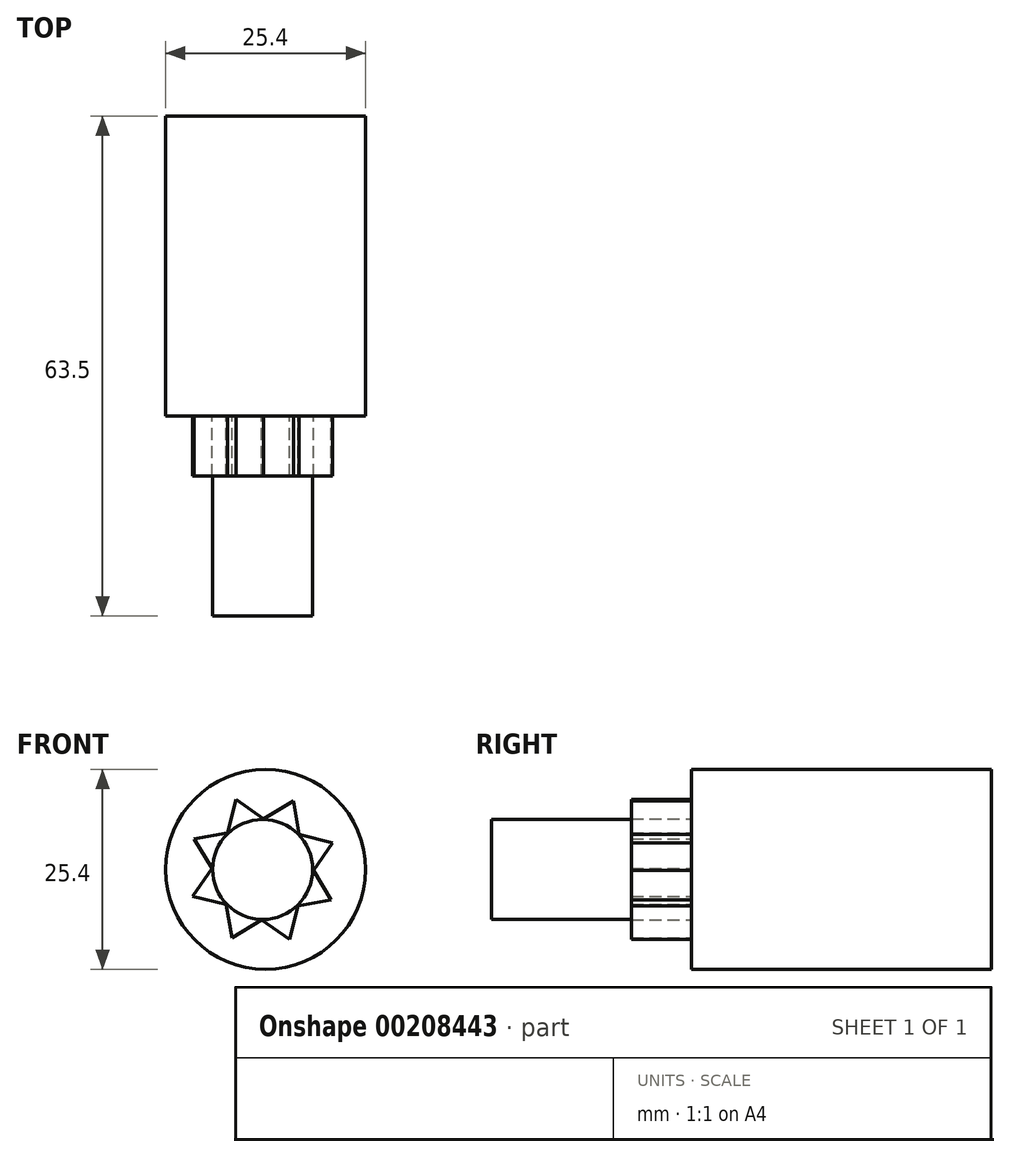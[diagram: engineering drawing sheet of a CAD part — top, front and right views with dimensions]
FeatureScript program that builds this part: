
annotation { "Feature Type Name" : "Feature", "Feature Type Description" : "" }
export const myFeature = defineFeature(function(context is Context, id is Id, definition is map)
    precondition{}
    {
        {
            var Q0;
            Q0=qCreatedBy(makeId("Front.planeOp"),FACE);
            var sketch = newSketch(context, id + "F0", { "sketchPlane" : qUnion([Q0])});
            skCircle(sketch, "E0", {"center": v(0.36, 0) * mm, "radius": 12.7 * mm});
            skSolve(sketch);
        }
        {
            var Q0;
            Q0=makeQuery(id+"F0.imprint","IMPRINT",FACE,{"disambiguationData":[TD([[makeQuery(id+"F0.imprint","IMPRINT",EDGE,{"derivedFrom":sQuery(id+"F0.wireOp",EDGE,"E0")}),1.0]])]});
            extrude(context, id + "F1", {"entities" : qUnion([Q0]), "depth" : 38.1 * mm});
        }
        {
            var Q0;
            Q0=makeQuery(id+"F1.opExtrude","CAP_FACE",FACE,{"disambiguationData":[OSD([sQuery(id+"F0.wireOp",EDGE,"E0")])],"isStart":false});
            var sketch = newSketch(context, id + "F2", { "sketchPlane" : qUnion([Q0])});
            skCircle(sketch, "E1", {"center": v(0, 0) * mm, "radius": 6.35 * mm});
            skSolve(sketch);
        }
        {
            var Q0;
            Q0=qSketchRegion(id+"F2",true);
            extrude(context, id + "F3", {"entities" : qUnion([Q0]), "operationType" : NewBodyOperationType.ADD, "depth" : 25.4 * mm});
        }
        {
            var Q0;
            Q0=makeQuery(id+"F1.opExtrude","CAP_FACE",FACE,{"disambiguationData":[OSD([sQuery(id+"F0.wireOp",EDGE,"E0")])],"isStart":false});
            var sketch = newSketch(context, id + "F4", { "sketchPlane" : qUnion([Q0])});
            skLineSegment(sketch, "E2", {"start": v(-8.7, 3.89) * mm, "end": v(-4.46, 4.63) * mm});
            skLineSegment(sketch, "E3", {"start": v(-8.7, 3.89) * mm, "end": v(-6.42, 0.12) * mm});
            skLineSegment(sketch, "E4.1.1", {"start": v(-8.9, -3.4) * mm, "end": v(-6.42, 0.12) * mm});
            skLineSegment(sketch, "E4.1.2", {"start": v(-8.9, -3.4) * mm, "end": v(-4.63, -4.46) * mm});
            skLineSegment(sketch, "E4.2.1", {"start": v(-3.89, -8.7) * mm, "end": v(-4.63, -4.46) * mm});
            skLineSegment(sketch, "E4.2.2", {"start": v(-3.89, -8.7) * mm, "end": v(-0.12, -6.42) * mm});
            skLineSegment(sketch, "E4.3.1", {"start": v(3.4, -8.9) * mm, "end": v(-0.12, -6.42) * mm});
            skLineSegment(sketch, "E4.3.2", {"start": v(3.4, -8.9) * mm, "end": v(4.46, -4.63) * mm});
            skLineSegment(sketch, "E4.4.1", {"start": v(8.7, -3.89) * mm, "end": v(4.46, -4.63) * mm});
            skLineSegment(sketch, "E4.4.2", {"start": v(8.7, -3.89) * mm, "end": v(6.42, -0.12) * mm});
            skLineSegment(sketch, "E4.5.1", {"start": v(8.9, 3.4) * mm, "end": v(6.42, -0.12) * mm});
            skLineSegment(sketch, "E4.5.2", {"start": v(8.9, 3.4) * mm, "end": v(4.63, 4.46) * mm});
            skLineSegment(sketch, "E4.6.1", {"start": v(3.89, 8.7) * mm, "end": v(4.63, 4.46) * mm});
            skLineSegment(sketch, "E4.6.2", {"start": v(3.89, 8.7) * mm, "end": v(0.12, 6.42) * mm});
            skLineSegment(sketch, "E4.7.1", {"start": v(-3.4, 8.9) * mm, "end": v(0.12, 6.42) * mm});
            skLineSegment(sketch, "E4.7.2", {"start": v(-3.4, 8.9) * mm, "end": v(-4.46, 4.63) * mm});
            skPoint(sketch, "E4.center", {"position": v(0, 0) * mm});
            skPoint(sketch, "E5.orphan", {"position": v(4.32, -4.65) * mm});
            skPoint(sketch, "E6.orphan", {"position": v(4.5, -4.5) * mm});
            skPoint(sketch, "E7.orphan", {"position": v(0, -6.35) * mm});
            skPoint(sketch, "E8.orphan", {"position": v(-4.5, -4.5) * mm});
            skPoint(sketch, "E9.orphan", {"position": v(-6.35, 0) * mm});
            skSolve(sketch);
        }
        {
            var Q0;
            Q0=makeQuery(id+"F4.imprint","IMPRINT",FACE,{"disambiguationData":[TD([[makeQuery(id+"F4.imprint","IMPRINT",EDGE,{"derivedFrom":makeQuery(id+"F3.opExtrude","CAP_EDGE",EDGE,{"disambiguationData":[OSD([sQuery(id+"F2.wireOp",EDGE,"E1")])],"isStart":true})}),1.0]])]});
            var Q1;
            Q1=makeQuery(id+"F4.imprint","IMPRINT",FACE,{"disambiguationData":[TD([[makeQuery(id+"F4.imprint","IMPRINT",EDGE,{"derivedFrom":sQuery(id+"F4.wireOp",EDGE,"E2")}),-1.0]])]});
            extrude(context, id + "F5", {"entities" : qUnion([Q0, Q1]), "operationType" : NewBodyOperationType.ADD, "depth" : 7.62 * mm});
        }
    });
